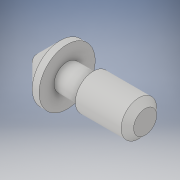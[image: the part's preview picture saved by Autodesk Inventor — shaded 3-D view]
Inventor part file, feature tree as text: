
AUTODESK INVENTOR PART (.ipt)
format: ipt  version: 2018.3 (Build 223284000, 284)  size: 124,928 bytes
history: native  units: in
note: dims shown in document units (in); Inventor stores cm internally (conversion verified against a paired STEP export)
features: revolve x1, sketch x1
ambient origin geometry x8: Origin, YZ Plane, XZ Plane, XY Plane, X Axis, Y Axis, Z Axis, Center Point
bodies: Solid1 (feature_tree)
feature tree (2):
  revolve  "Revolution1"  [1 undecoded]
  sketch  "Sketch1"  dims[d0=0.53in d1=0.06in d2=45.0deg d3=0.135in d4=0.0855in d5=0.25in d6=0.0625in d7=0.375in d8=0.03in d9=0.03in d10=90.0deg]
note: 1 required parameter value undecoded (feature->parameter linkage not recoverable at this tier; creation-order binding heuristic only, values carry confidence <= 0.55)
